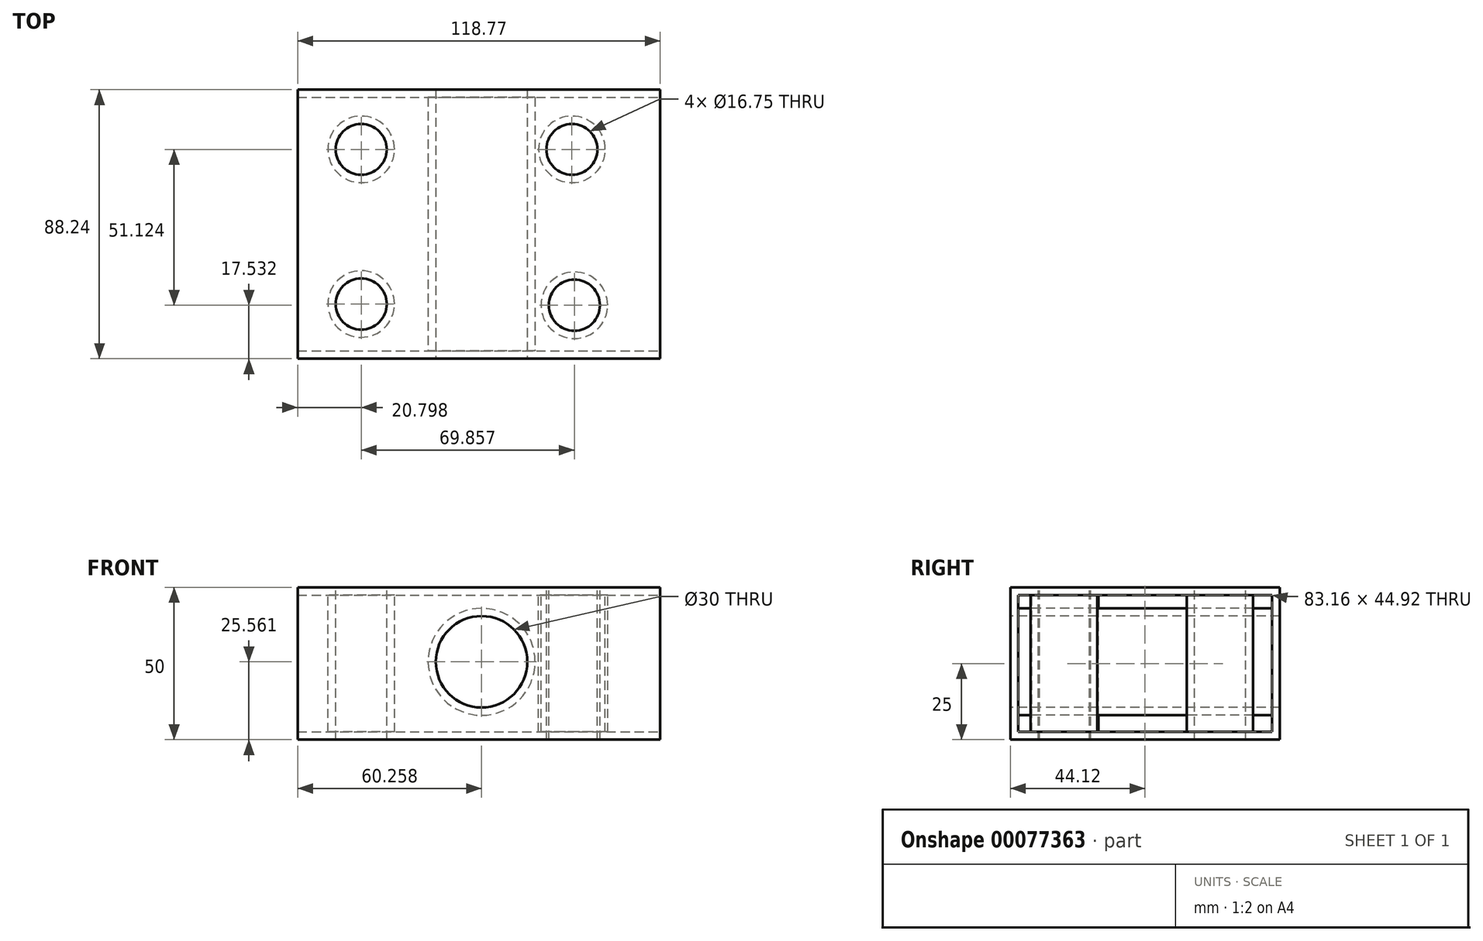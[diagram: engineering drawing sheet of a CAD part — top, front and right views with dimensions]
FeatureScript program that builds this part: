
annotation { "Feature Type Name" : "Feature", "Feature Type Description" : "" }
export const myFeature = defineFeature(function(context is Context, id is Id, definition is map)
    precondition{}
    {
        {
            var Q0;
            Q0=qCreatedBy(makeId("Top.planeOp"),FACE);
            var sketch = newSketch(context, id + "F0", { "sketchPlane" : qUnion([Q0])});
            skLineSegment(sketch, "E0.bottom", {"start": v(-62.53, 47.82) * mm, "end": v(56.24, 47.82) * mm});
            skLineSegment(sketch, "E0.top", {"start": v(-62.53, -40.42) * mm, "end": v(56.24, -40.42) * mm});
            skLineSegment(sketch, "E0.left", {"start": v(-62.53, 47.82) * mm, "end": v(-62.53, -40.42) * mm});
            skLineSegment(sketch, "E0.right", {"start": v(56.24, 47.82) * mm, "end": v(56.24, -40.42) * mm});
            skSolve(sketch);
        }
        {
            var Q0;
            Q0 = qSketchRegion(id + "F0", true);
            extrude(context, id + "F1", {"entities" : qUnion([Q0]), "depth" : 50 * mm});
        }
        {
            var Q0;
            Q0=makeQuery(id+"F1.opExtrude","CAP_FACE",FACE,{"disambiguationData":[OSD([sQuery(id+"F0.wireOp",EDGE,"E0.bottom"),sQuery(id+"F0.wireOp",EDGE,"E0.top"),sQuery(id+"F0.wireOp",EDGE,"E0.left"),sQuery(id+"F0.wireOp",EDGE,"E0.right")])],"isStart":false});
            var sketch = newSketch(context, id + "F2", { "sketchPlane" : qUnion([Q0])});
            skCircle(sketch, "E1", {"center": v(-41.73, 28.24) * mm, "radius": 13 * mm});
            skCircle(sketch, "E2", {"center": v(-41.73, -22.5) * mm, "radius": 15.74 * mm});
            skCircle(sketch, "E3", {"center": v(28.12, -22.89) * mm, "radius": 14 * mm});
            skCircle(sketch, "E4", {"center": v(27.34, 28.24) * mm, "radius": 14.24 * mm});
            skSolve(sketch);
        }
        {
            var Q0;
            Q0=sQuery(id+"F2.wireOp",VERTEX,"E1.center");
            var Q1;
            Q1=sQuery(id+"F2.wireOp",VERTEX,"E4.center");
            var Q2;
            Q2=sQuery(id+"F2.wireOp",VERTEX,"E3.center");
            var Q3;
            Q3=sQuery(id+"F2.wireOp",VERTEX,"E2.center");
            var Q4;
            Q4=makeQuery(id+"F1.opExtrude","SWEPT_BODY",BODY,{"disambiguationData":[OSD([sQuery(id+"F0.wireOp",EDGE,"E0.bottom"),sQuery(id+"F0.wireOp",EDGE,"E0.top"),sQuery(id+"F0.wireOp",EDGE,"E0.left"),sQuery(id+"F0.wireOp",EDGE,"E0.right")])]});
            hole(context, id + "F3", {"style" : HoleStyle.SIMPLE, "endStyle" : HoleEndStyle.THROUGH, "standardTappedOrClearance" : lookupTablePath({ "standard" : "ISO", "fit" : "Close", "size" : "M16", "type" : "Clearance" }), "standardBlindInLast" : lookupTablePath({ "fit" : "Close", "standard" : "ISO", "size" : "M16", "type" : "Clearance" }), "holeDiameter" : 16.75 * mm, "startFromSketch" : true, "locations" : qUnion([Q0, Q1, Q2, Q3]), "scope" : qUnion([Q4]), "isTappedThrough" : true});
        }
        {
            var Q0;
            Q0=makeQuery(id+"F1.opExtrude","SWEPT_FACE",FACE,{"disambiguationData":[OSD([sQuery(id+"F0.wireOp",EDGE,"E0.top")])]});
            var sketch = newSketch(context, id + "F4", { "sketchPlane" : qUnion([Q0])});
            skCircle(sketch, "E5", {"center": v(-2.27, 25.56) * mm, "radius": 16.38 * mm});
            skSolve(sketch);
        }
        {
            var Q0;
            Q0=sQuery(id+"F4.wireOp",VERTEX,"E5.center");
            var Q1;
            Q1=makeQuery(id+"F1.opExtrude","SWEPT_BODY",BODY,{"disambiguationData":[OSD([sQuery(id+"F0.wireOp",EDGE,"E0.bottom"),sQuery(id+"F0.wireOp",EDGE,"E0.top"),sQuery(id+"F0.wireOp",EDGE,"E0.left"),sQuery(id+"F0.wireOp",EDGE,"E0.right")])]});
            hole(context, id + "F5", {"style" : HoleStyle.SIMPLE, "endStyle" : HoleEndStyle.THROUGH, "holeDiameter" : 30 * mm, "startFromSketch" : true, "locations" : qUnion([Q0]), "scope" : qUnion([Q1]), "isTappedThrough" : true});
        }
        {
            var Q0;
            Q0=makeQuery(id+"F1.opExtrude","SWEPT_FACE",FACE,{"disambiguationData":[OSD([sQuery(id+"F0.wireOp",EDGE,"E0.right")])]});
            var Q1;
            Q1=makeQuery(id+"F1.opExtrude","SWEPT_FACE",FACE,{"disambiguationData":[OSD([sQuery(id+"F0.wireOp",EDGE,"E0.left")])]});
            var Q2;
            Q2=makeQuery(id+"F1.opExtrude","SWEPT_BODY",BODY,{"disambiguationData":[OSD([sQuery(id+"F0.wireOp",EDGE,"E0.bottom"),sQuery(id+"F0.wireOp",EDGE,"E0.top"),sQuery(id+"F0.wireOp",EDGE,"E0.left"),sQuery(id+"F0.wireOp",EDGE,"E0.right")])]});
            shell(context, id + "F6", {"entities" : qUnion([Q0, Q1]), "parts" : qUnion([Q2]), "thickness" : 2.54 * mm});
        }
    });
